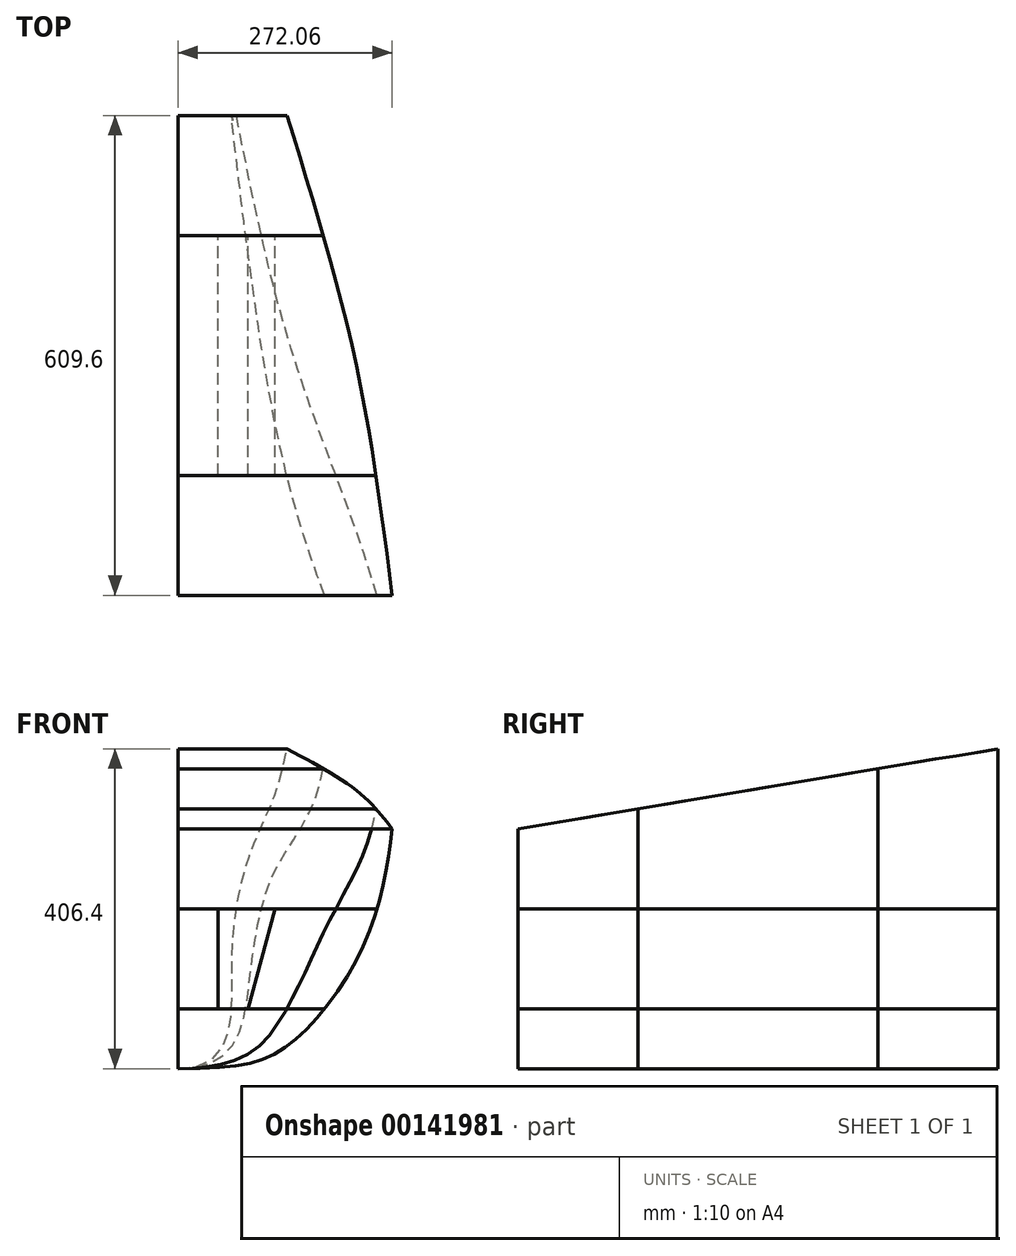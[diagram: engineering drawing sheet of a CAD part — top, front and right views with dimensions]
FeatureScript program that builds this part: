
annotation { "Feature Type Name" : "Feature", "Feature Type Description" : "" }
export const myFeature = defineFeature(function(context is Context, id is Id, definition is map)
    precondition{}
    {
        {
            var Q0;
            Q0=qCreatedBy(makeId("Front.planeOp"),FACE);
            cPlane(context, id + "F0", {"entities" : qUnion([Q0]), "cplaneType" : CPlaneType.OFFSET, "offset" : 304.8 * mm, "oppositeDirection" : true, "width" : 152.4 * mm, "height" : 152.4 * mm});
        }
        {
            var Q0;
            Q0=qCreatedBy(id+"F0.planeOp",FACE);
            cPlane(context, id + "F1", {"entities" : qUnion([Q0]), "cplaneType" : CPlaneType.OFFSET, "offset" : 304.8 * mm, "oppositeDirection" : true, "width" : 152.4 * mm, "height" : 152.4 * mm});
        }
        {
            var Q0;
            Q0=qCreatedBy(makeId("Front.planeOp"),FACE);
            var sketch = newSketch(context, id + "F2", { "sketchPlane" : qUnion([Q0])});
            skLineSegment(sketch, "E0", {"start": v(0, 0) * mm, "end": v(0, 304.8) * mm, "construction": true});
            skFitSpline(sketch, "E1", {"points": [v(0, 0) * mm, v(143.42, 32.46) * mm, v(239.96, 166.78) * mm, v(272.06, 304.8) * mm], "startDerivative": vector(695.45, 0) * mm, "endDerivative": vector(48.6, 386.92) * mm});
            skLineSegment(sketch, "E2", {"start": v(0, 0) * mm, "end": v(76.2, 0) * mm, "construction": true});
            skSolve(sketch);
        }
        {
            var Q0;
            Q0=qCreatedBy(id+"F0.planeOp",FACE);
            var sketch = newSketch(context, id + "F3", { "sketchPlane" : qUnion([Q0])});
            skLineSegment(sketch, "E3", {"start": v(0, 0) * mm, "end": v(0, 355.6) * mm, "construction": true});
            skFitSpline(sketch, "E4", {"points": [v(0, 0) * mm, v(109.21, 80.73) * mm, v(153.74, 218.95) * mm, v(223.62, 355.6) * mm], "startDerivative": vector(708, 0) * mm, "endDerivative": vector(92.69, 549.76) * mm});
            skLineSegment(sketch, "E5", {"start": v(0, 0) * mm, "end": v(76.2, 0) * mm, "construction": true});
            skSolve(sketch);
        }
        {
            var Q0;
            Q0=qCreatedBy(id+"F1.planeOp",FACE);
            var sketch = newSketch(context, id + "F4", { "sketchPlane" : qUnion([Q0])});
            skLineSegment(sketch, "E6", {"start": v(0, 0) * mm, "end": v(0, 406.4) * mm, "construction": true});
            skFitSpline(sketch, "E7", {"points": [v(0, 0) * mm, v(68.37, 129.21) * mm, v(94.25, 280.24) * mm, v(138.2, 406.4) * mm], "startDerivative": vector(681.17, 0) * mm, "endDerivative": vector(92.69, 549.76) * mm});
            skLineSegment(sketch, "E8", {"start": v(0, 0) * mm, "end": v(76.2, 0) * mm, "construction": true});
            skSolve(sketch);
        }
        {
            var Q0;
            Q0 = qConstructionFilter(qBodyType(qCreatedBy(id + "F2" ,EDGE), BodyType.WIRE), ConstructionObject.NO);
            var Q1;
            Q1 = qConstructionFilter(qBodyType(qCreatedBy(id + "F3" ,EDGE), BodyType.WIRE), ConstructionObject.NO);
            var Q2;
            Q2 = qConstructionFilter(qBodyType(qCreatedBy(id + "F4" ,EDGE), BodyType.WIRE), ConstructionObject.NO);
            loft(context, id + "F5", {"bodyType" : ToolBodyType.SURFACE, "wireProfilesArray" : [{ "wireProfileEntities" : qUnion([Q0]) }, { "wireProfileEntities" : qUnion([Q1]) }, { "wireProfileEntities" : qUnion([Q2]) }]});
        }
        {
            var Q0;
            Q0=qCreatedBy(makeId("Right.planeOp"),FACE);
            var sketch = newSketch(context, id + "F6", { "sketchPlane" : qUnion([Q0])});
            skFitSpline(sketch, "E9.0", {"points": [v(0, 0) * mm, v(0, 101.6) * mm, v(0, 203.2) * mm, v(0, 304.8) * mm], "construction": true});
            skFitSpline(sketch, "E9.1", {"points": [v(609.6, 406.4) * mm, v(609.6, 270.93) * mm, v(609.6, 135.47) * mm, v(609.6, 0) * mm], "construction": true});
            skFitSpline(sketch, "E9.2", {"points": [v(609.6, 0) * mm, v(508, 0) * mm, v(406.4, 0) * mm, v(304.8, 0) * mm], "construction": true});
            skFitSpline(sketch, "E9.3", {"points": [v(304.8, 0) * mm, v(203.2, 0) * mm, v(101.6, 0) * mm, v(0, 0) * mm], "construction": true});
            skLineSegment(sketch, "E10", {"start": v(0, 76.2) * mm, "end": v(609.6, 76.2) * mm});
            skSolve(sketch);
        }
        {
            var Q0;
            Q0 = qSketchRegion(id + "F6", true);
            var Q1;
            Q1 = qConstructionFilter(qBodyType(qCreatedBy(id + "F6" ,EDGE), BodyType.WIRE), ConstructionObject.NO);
            var Q2;
            Q2=makeQuery(id+"F5.opLoft","SWEPT_FACE",FACE,{"disambiguationData":[OSD([sQuery(id+"F2.wireOp",VERTEX,"E1.start"),sQuery(id+"F2.wireOp",VERTEX,"E1.end"),sQuery(id+"F2.wireOp",EDGE,"E1"),sQuery(id+"F3.wireOp",VERTEX,"E4.start"),sQuery(id+"F3.wireOp",VERTEX,"E4.end"),sQuery(id+"F3.wireOp",EDGE,"E4")])]});
            extrude(context, id + "F7", {"entities" : qUnion([Q0]), "bodyType" : ToolBodyType.SURFACE, "surfaceEntities" : qUnion([Q1]), "endBound" : BoundingType.UP_TO_SURFACE, "endBoundEntityFace" : qUnion([Q2]), "depth" : 25.4 * mm});
        }
        {
            var Q0;
            Q0=qCreatedBy(makeId("Right.planeOp"),FACE);
            var sketch = newSketch(context, id + "F8", { "sketchPlane" : qUnion([Q0])});
            skFitSpline(sketch, "E11.0", {"points": [v(0, 0) * mm, v(0, 101.6) * mm, v(0, 203.2) * mm, v(0, 304.8) * mm], "construction": true});
            skFitSpline(sketch, "E11.1", {"points": [v(304.8, 0) * mm, v(203.2, 0) * mm, v(101.6, 0) * mm, v(0, 0) * mm], "construction": true});
            skFitSpline(sketch, "E11.2", {"points": [v(609.6, 0) * mm, v(508, 0) * mm, v(406.4, 0) * mm, v(304.8, 0) * mm], "construction": true});
            skFitSpline(sketch, "E11.3", {"points": [v(609.6, 406.4) * mm, v(609.6, 270.93) * mm, v(609.6, 135.47) * mm, v(609.6, 0) * mm], "construction": true});
            skLineSegment(sketch, "E12", {"start": v(0, 203.2) * mm, "end": v(609.6, 203.2) * mm});
            skSolve(sketch);
        }
        {
            var Q0;
            Q0 = qConstructionFilter(qBodyType(qCreatedBy(id + "F8" ,EDGE), BodyType.WIRE), ConstructionObject.NO);
            var Q1;
            Q1=makeQuery(id+"F5.opLoft","SWEPT_FACE",FACE,{"disambiguationData":[OSD([sQuery(id+"F2.wireOp",VERTEX,"E1.start"),sQuery(id+"F2.wireOp",VERTEX,"E1.end"),sQuery(id+"F2.wireOp",EDGE,"E1"),sQuery(id+"F3.wireOp",VERTEX,"E4.start"),sQuery(id+"F3.wireOp",VERTEX,"E4.end"),sQuery(id+"F3.wireOp",EDGE,"E4")])]});
            extrude(context, id + "F9", {"bodyType" : ToolBodyType.SURFACE, "surfaceEntities" : qUnion([Q0]), "endBound" : BoundingType.UP_TO_SURFACE, "endBoundEntityFace" : qUnion([Q1]), "depth" : 25.4 * mm});
        }
        {
            var Q0;
            Q0=qCreatedBy(makeId("Right.planeOp"),FACE);
            var sketch = newSketch(context, id + "F10", { "sketchPlane" : qUnion([Q0])});
            skFitSpline(sketch, "E13.0", {"points": [v(0, 0) * mm, v(0, 101.6) * mm, v(0, 203.2) * mm, v(0, 304.8) * mm], "construction": true});
            skFitSpline(sketch, "E13.1", {"points": [v(304.8, 0) * mm, v(203.2, 0) * mm, v(101.6, 0) * mm, v(0, 0) * mm], "construction": true});
            skFitSpline(sketch, "E13.2", {"points": [v(609.6, 0) * mm, v(508, 0) * mm, v(406.4, 0) * mm, v(304.8, 0) * mm], "construction": true});
            skFitSpline(sketch, "E13.3", {"points": [v(609.6, 406.4) * mm, v(609.6, 270.93) * mm, v(609.6, 135.47) * mm, v(609.6, 0) * mm], "construction": true});
            skLineSegment(sketch, "E14", {"start": v(0, 304.8) * mm, "end": v(609.6, 406.4) * mm});
            skSolve(sketch);
        }
        {
            var Q0;
            Q0 = qSketchRegion(id + "F10", true);
            var Q1;
            Q1 = qConstructionFilter(qBodyType(qCreatedBy(id + "F10" ,EDGE), BodyType.WIRE), ConstructionObject.NO);
            var Q2;
            Q2=makeQuery(id+"F5.opLoft","SWEPT_FACE",FACE,{"disambiguationData":[OSD([sQuery(id+"F2.wireOp",VERTEX,"E1.start"),sQuery(id+"F2.wireOp",VERTEX,"E1.end"),sQuery(id+"F2.wireOp",EDGE,"E1"),sQuery(id+"F3.wireOp",VERTEX,"E4.start"),sQuery(id+"F3.wireOp",VERTEX,"E4.end"),sQuery(id+"F3.wireOp",EDGE,"E4")])]});
            extrude(context, id + "F11", {"entities" : qUnion([Q0]), "bodyType" : ToolBodyType.SURFACE, "surfaceEntities" : qUnion([Q1]), "endBound" : BoundingType.UP_TO_SURFACE, "endBoundEntityFace" : qUnion([Q2]), "depth" : 25.4 * mm});
        }
        {
            var Q0;
            Q0=qCreatedBy(makeId("Right.planeOp"),FACE);
            var sketch = newSketch(context, id + "F12", { "sketchPlane" : qUnion([Q0])});
            skFitSpline(sketch, "E15.0", {"points": [v(0, 304.8) * mm, v(101.6, 321.73) * mm, v(203.2, 338.67) * mm, v(304.8, 355.6) * mm], "construction": true});
            skFitSpline(sketch, "E15.1", {"points": [v(304.8, 355.6) * mm, v(406.4, 372.53) * mm, v(508, 389.47) * mm, v(609.6, 406.4) * mm], "construction": true});
            skFitSpline(sketch, "E15.2", {"points": [v(609.6, 0) * mm, v(508, 0) * mm, v(406.4, 0) * mm, v(304.8, 0) * mm], "construction": true});
            skFitSpline(sketch, "E15.3", {"points": [v(304.8, 0) * mm, v(203.2, 0) * mm, v(101.6, 0) * mm, v(0, 0) * mm], "construction": true});
            skFitSpline(sketch, "E15.4", {"points": [v(0, 0) * mm, v(0, 101.6) * mm, v(0, 203.2) * mm, v(0, 304.8) * mm], "construction": true});
            skFitSpline(sketch, "E15.5", {"points": [v(609.6, 406.4) * mm, v(609.6, 270.93) * mm, v(609.6, 135.47) * mm, v(609.6, 0) * mm], "construction": true});
            skLineSegment(sketch, "E16", {"start": v(152.4, 0) * mm, "end": v(152.4, 330.2) * mm});
            skLineSegment(sketch, "E17", {"start": v(457.2, 0) * mm, "end": v(457.2, 381) * mm});
            skSolve(sketch);
        }
        {
            var Q0;
            Q0 = qSketchRegion(id + "F12", true);
            var Q1;
            Q1 = qConstructionFilter(qBodyType(qCreatedBy(id + "F12" ,EDGE), BodyType.WIRE), ConstructionObject.NO);
            var Q2;
            Q2=makeQuery(id+"F5.opLoft","SWEPT_FACE",FACE,{"disambiguationData":[OSD([sQuery(id+"F2.wireOp",VERTEX,"E1.start"),sQuery(id+"F2.wireOp",VERTEX,"E1.end"),sQuery(id+"F2.wireOp",EDGE,"E1"),sQuery(id+"F3.wireOp",VERTEX,"E4.start"),sQuery(id+"F3.wireOp",VERTEX,"E4.end"),sQuery(id+"F3.wireOp",EDGE,"E4")])]});
            extrude(context, id + "F13", {"entities" : qUnion([Q0]), "bodyType" : ToolBodyType.SURFACE, "surfaceEntities" : qUnion([Q1]), "endBound" : BoundingType.UP_TO_SURFACE, "endBoundEntityFace" : qUnion([Q2]), "depth" : 25.4 * mm});
        }
        {
            var Q0;
            Q0=makeQuery(id+"F13.opExtrude","SWEPT_FACE",FACE,{"disambiguationData":[OSD([sQuery(id+"F12.wireOp",EDGE,"E16")])]});
            var sketch = newSketch(context, id + "F14", { "sketchPlane" : qUnion([Q0])});
            skLineSegment(sketch, "E18.0", {"start": v(-186.14, 76.2) * mm, "end": v(0, 76.2) * mm, "construction": true});
            skLineSegment(sketch, "E18.1", {"start": v(-252.9, 203.2) * mm, "end": v(0, 203.2) * mm, "construction": true});
            skLineSegment(sketch, "E18.2", {"start": v(0, 330.2) * mm, "end": v(-251.3, 330.2) * mm, "construction": true});
            skLineSegment(sketch, "E19", {"start": v(-50.8, 76.2) * mm, "end": v(-50.8, 203.2) * mm});
            skLineSegment(sketch, "E20", {"start": v(-88.9, 76.2) * mm, "end": v(-122.93, 203.2) * mm});
            skLineSegment(sketch, "E21", {"start": v(-88.9, 76.2) * mm, "end": v(-88.9, 203.2) * mm, "construction": true});
            skSolve(sketch);
        }
        {
            var Q0;
            Q0 = qSketchRegion(id + "F14", true);
            var Q1;
            Q1 = qConstructionFilter(qBodyType(qCreatedBy(id + "F14" ,EDGE), BodyType.WIRE), ConstructionObject.NO);
            var Q2;
            Q2=makeQuery(id+"F13.opExtrude","SWEPT_FACE",FACE,{"disambiguationData":[OSD([sQuery(id+"F12.wireOp",EDGE,"E17")])]});
            extrude(context, id + "F15", {"entities" : qUnion([Q0]), "bodyType" : ToolBodyType.SURFACE, "surfaceEntities" : qUnion([Q1]), "endBound" : BoundingType.UP_TO_SURFACE, "endBoundEntityFace" : qUnion([Q2]), "depth" : 25.4 * mm});
        }
    });
